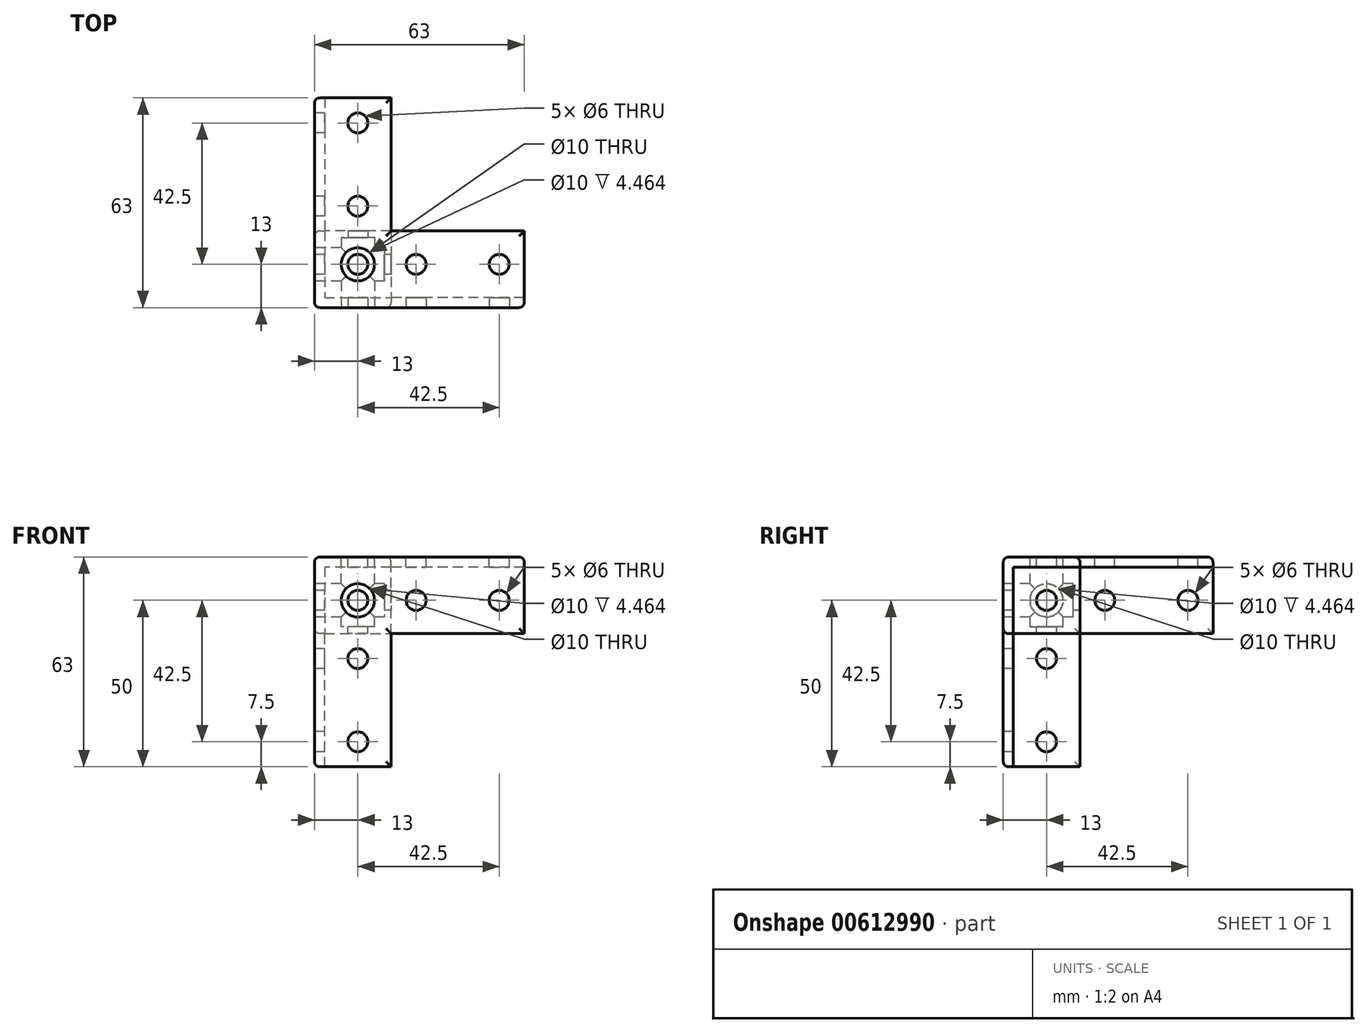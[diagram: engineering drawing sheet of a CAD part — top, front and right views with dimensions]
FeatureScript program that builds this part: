
annotation { "Feature Type Name" : "Feature", "Feature Type Description" : "" }
export const myFeature = defineFeature(function(context is Context, id is Id, definition is map)
    precondition{}
    {
        {
            var Q0;
            Q0=qCreatedBy(makeId("Front.planeOp"),FACE);
            var sketch = newSketch(context, id + "F0", { "sketchPlane" : qUnion([Q0])});
            skLineSegment(sketch, "E0", {"start": v(0, 0) * mm, "end": v(0, 40) * mm});
            skLineSegment(sketch, "E1", {"start": v(0, 0) * mm, "end": v(-20, 0) * mm});
            skLineSegment(sketch, "E2", {"start": v(-20, 0) * mm, "end": v(-20, 40) * mm});
            skLineSegment(sketch, "E3", {"start": v(-20, 40) * mm, "end": v(0, 40) * mm});
            skLineSegment(sketch, "E4", {"start": v(-20, 40) * mm, "end": v(-23, 40) * mm});
            skLineSegment(sketch, "E5", {"start": v(-23, 40) * mm, "end": v(-23, 0) * mm});
            skLineSegment(sketch, "E6", {"start": v(-23, 0) * mm, "end": v(-20, 0) * mm});
            skCircle(sketch, "E7", {"center": v(-10, 32.5) * mm, "radius": 3 * mm});
            skCircle(sketch, "E8", {"center": v(-10, 7.5) * mm, "radius": 3 * mm});
            skLineSegment(sketch, "E9", {"start": v(-10, 40) * mm, "end": v(-10, 0) * mm, "construction": true});
            skLineSegment(sketch, "E10", {"start": v(0, 40) * mm, "end": v(0, 60) * mm});
            skLineSegment(sketch, "E11", {"start": v(0, 60) * mm, "end": v(-20, 60) * mm});
            skLineSegment(sketch, "E12", {"start": v(-20, 60) * mm, "end": v(-20, 40) * mm});
            skLineSegment(sketch, "E13", {"start": v(-23, 40) * mm, "end": v(-23, 60) * mm});
            skLineSegment(sketch, "E14", {"start": v(-23, 60) * mm, "end": v(-20, 60) * mm});
            skLineSegment(sketch, "E15", {"start": v(0, 60) * mm, "end": v(40, 60) * mm});
            skLineSegment(sketch, "E16", {"start": v(40, 60) * mm, "end": v(40, 40) * mm});
            skLineSegment(sketch, "E17", {"start": v(40, 40) * mm, "end": v(0, 40) * mm});
            skLineSegment(sketch, "E18", {"start": v(-20, 50) * mm, "end": v(40, 50) * mm, "construction": true});
            skCircle(sketch, "E19", {"center": v(7.5, 50) * mm, "radius": 3 * mm});
            skCircle(sketch, "E20", {"center": v(32.5, 50) * mm, "radius": 3 * mm});
            skCircle(sketch, "E21", {"center": v(-10, 50) * mm, "radius": 5 * mm});
            skLineSegment(sketch, "E22", {"start": v(-23, 60) * mm, "end": v(-23, 63) * mm});
            skLineSegment(sketch, "E23", {"start": v(-23, 63) * mm, "end": v(40, 63) * mm});
            skLineSegment(sketch, "E24", {"start": v(40, 63) * mm, "end": v(40, 60) * mm});
            skLineSegment(sketch, "E25", {"start": v(0, 60) * mm, "end": v(0, 63) * mm});
            skSolve(sketch);
        }
        {
            var Q0;
            Q0=makeQuery(id+"F0.imprint","IMPRINT",FACE,{"disambiguationData":[TD([[makeQuery(id+"F0.imprint","IMPRINT",EDGE,{"derivedFrom":sQuery(id+"F0.wireOp",EDGE,"E0")}),1.0]])]});
            var Q1;
            Q1=makeQuery(id+"F0.imprint","IMPRINT",FACE,{"disambiguationData":[TD([[makeQuery(id+"F0.imprint","IMPRINT",EDGE,{"derivedFrom":sQuery(id+"F0.wireOp",EDGE,"E3")}),1.0]])]});
            var Q2;
            Q2=makeQuery(id+"F0.imprint","IMPRINT",FACE,{"disambiguationData":[TD([[makeQuery(id+"F0.imprint","IMPRINT",EDGE,{"derivedFrom":sQuery(id+"F0.wireOp",EDGE,"E10")}),-1.0]])]});
            extrude(context, id + "F1", {"entities" : qUnion([Q0, Q1, Q2]), "oppositeDirection" : true, "depth" : 3 * mm, "offsetDistance" : 25 * mm});
        }
        {
            var Q0;
            Q0=makeQuery(id+"F0.imprint","IMPRINT",FACE,{"disambiguationData":[TD([[makeQuery(id+"F0.imprint","IMPRINT",EDGE,{"derivedFrom":sQuery(id+"F0.wireOp",EDGE,"E2")}),1.0]])]});
            var Q1;
            Q1=makeQuery(id+"F0.imprint","IMPRINT",FACE,{"disambiguationData":[TD([[makeQuery(id+"F0.imprint","IMPRINT",EDGE,{"derivedFrom":sQuery(id+"F0.wireOp",EDGE,"E15")}),1.0]])]});
            extrude(context, id + "F2", {"entities" : qUnion([Q0, Q1]), "operationType" : NewBodyOperationType.ADD, "oppositeDirection" : true, "depth" : 23 * mm, "offsetDistance" : 25 * mm});
        }
        {
            var Q0;
            Q0=makeQuery(id+"F0.imprint","IMPRINT",FACE,{"disambiguationData":[TD([[makeQuery(id+"F0.imprint","IMPRINT",EDGE,{"derivedFrom":sQuery(id+"F0.wireOp",EDGE,"E11")}),-1.0]])]});
            var Q1;
            Q1=makeQuery(id+"F0.imprint","IMPRINT",FACE,{"disambiguationData":[TD([[makeQuery(id+"F0.imprint","IMPRINT",EDGE,{"derivedFrom":sQuery(id+"F0.wireOp",EDGE,"E4")}),-1.0]])]});
            extrude(context, id + "F3", {"entities" : qUnion([Q0, Q1]), "operationType" : NewBodyOperationType.ADD, "oppositeDirection" : true, "depth" : 63 * mm, "offsetDistance" : 25 * mm});
        }
        {
            var Q0;
            {var subQ0=sQuery(id+"F0.wireOp",EDGE,"E23");Q0=makeQuery(id+"F3.boolean.opBoolean","MERGE",FACE,{"derivedFrom":[makeQuery(id+"F2.opExtrude","SWEPT_FACE",FACE,{"disambiguationData":[OSD([subQ0])]}),makeQuery(id+"F3.opExtrude","SWEPT_FACE",FACE,{"disambiguationData":[OSD([subQ0])]})]});}
            var sketch = newSketch(context, id + "F4", { "sketchPlane" : qUnion([Q0])});
            skCircle(sketch, "E26", {"center": v(-10, 55.5) * mm, "radius": 3 * mm});
            skCircle(sketch, "E27", {"center": v(-10, 30.5) * mm, "radius": 3 * mm});
            skCircle(sketch, "E28", {"center": v(-10, 13) * mm, "radius": 5 * mm});
            skCircle(sketch, "E29", {"center": v(7.5, 13) * mm, "radius": 3 * mm});
            skCircle(sketch, "E30", {"center": v(32.5, 13) * mm, "radius": 3 * mm});
            skLineSegment(sketch, "E31", {"start": v(-10, 63) * mm, "end": v(-10, 0) * mm, "construction": true});
            skLineSegment(sketch, "E32", {"start": v(40, 13) * mm, "end": v(-10, 13) * mm, "construction": true});
            skLineSegment(sketch, "E33", {"start": v(0, 23) * mm, "end": v(0, 0) * mm, "construction": true});
            skSolve(sketch);
        }
        {
            var Q0;
            Q0=makeQuery(id+"F3.boolean.opBoolean","MERGE",FACE,{"derivedFrom":[makeQuery(id+"F2.opExtrude","SWEPT_FACE",FACE,{"disambiguationData":[OSD([sQuery(id+"F0.wireOp",EDGE,"E5")])]}),makeQuery(id+"F3.opExtrude","SWEPT_FACE",FACE,{"disambiguationData":[OSD([sQuery(id+"F0.wireOp",EDGE,"E13"),sQuery(id+"F0.wireOp",EDGE,"E22")])]})]});
            var sketch = newSketch(context, id + "F5", { "sketchPlane" : qUnion([Q0])});
            skLineSegment(sketch, "E34", {"start": v(-63, 50) * mm, "end": v(0, 50) * mm, "construction": true});
            skLineSegment(sketch, "E35", {"start": v(-13, 0) * mm, "end": v(-13, 50) * mm, "construction": true});
            skLineSegment(sketch, "E36", {"start": v(-23, 40) * mm, "end": v(0, 40) * mm, "construction": true});
            skLineSegment(sketch, "E37", {"start": v(-23, 40) * mm, "end": v(-23, 63) * mm, "construction": true});
            skCircle(sketch, "E38", {"center": v(-13, 50) * mm, "radius": 5 * mm});
            skCircle(sketch, "E39", {"center": v(-30.5, 50) * mm, "radius": 3 * mm});
            skCircle(sketch, "E40", {"center": v(-55.5, 50) * mm, "radius": 3 * mm});
            skCircle(sketch, "E41", {"center": v(-13, 32.5) * mm, "radius": 3 * mm});
            skCircle(sketch, "E42", {"center": v(-13, 7.5) * mm, "radius": 3 * mm});
            skSolve(sketch);
        }
        {
            var Q0;
            Q0=makeQuery(id+"F4.imprint","IMPRINT",FACE,{"disambiguationData":[TD([[makeQuery(id+"F4.imprint","IMPRINT",EDGE,{"derivedFrom":sQuery(id+"F4.wireOp",EDGE,"E26")}),1.0]])]});
            var Q1;
            Q1=makeQuery(id+"F4.imprint","IMPRINT",FACE,{"disambiguationData":[TD([[makeQuery(id+"F4.imprint","IMPRINT",EDGE,{"derivedFrom":sQuery(id+"F4.wireOp",EDGE,"E27")}),1.0]])]});
            var Q2;
            Q2=makeQuery(id+"F4.imprint","IMPRINT",FACE,{"disambiguationData":[TD([[makeQuery(id+"F4.imprint","IMPRINT",EDGE,{"derivedFrom":sQuery(id+"F4.wireOp",EDGE,"E28")}),1.0]])]});
            var Q3;
            Q3=makeQuery(id+"F4.imprint","IMPRINT",FACE,{"disambiguationData":[TD([[makeQuery(id+"F4.imprint","IMPRINT",EDGE,{"derivedFrom":sQuery(id+"F4.wireOp",EDGE,"E29")}),1.0]])]});
            var Q4;
            Q4=makeQuery(id+"F4.imprint","IMPRINT",FACE,{"disambiguationData":[TD([[makeQuery(id+"F4.imprint","IMPRINT",EDGE,{"derivedFrom":sQuery(id+"F4.wireOp",EDGE,"E30")}),1.0]])]});
            extrude(context, id + "F6", {"entities" : qUnion([Q0, Q1, Q2, Q3, Q4]), "operationType" : NewBodyOperationType.REMOVE, "oppositeDirection" : true, "depth" : 25 * mm, "offsetDistance" : 25 * mm});
        }
        {
            var Q0;
            Q0=makeQuery(id+"F5.imprint","IMPRINT",FACE,{"disambiguationData":[TD([[makeQuery(id+"F5.imprint","IMPRINT",EDGE,{"derivedFrom":sQuery(id+"F5.wireOp",EDGE,"E40")}),1.0]])]});
            var Q1;
            Q1=makeQuery(id+"F5.imprint","IMPRINT",FACE,{"disambiguationData":[TD([[makeQuery(id+"F5.imprint","IMPRINT",EDGE,{"derivedFrom":sQuery(id+"F5.wireOp",EDGE,"E39")}),1.0]])]});
            var Q2;
            Q2=makeQuery(id+"F5.imprint","IMPRINT",FACE,{"disambiguationData":[TD([[makeQuery(id+"F5.imprint","IMPRINT",EDGE,{"derivedFrom":sQuery(id+"F5.wireOp",EDGE,"E38")}),1.0]])]});
            var Q3;
            Q3=makeQuery(id+"F5.imprint","IMPRINT",FACE,{"disambiguationData":[TD([[makeQuery(id+"F5.imprint","IMPRINT",EDGE,{"derivedFrom":sQuery(id+"F5.wireOp",EDGE,"E42")}),1.0]])]});
            var Q4;
            Q4=makeQuery(id+"F5.imprint","IMPRINT",FACE,{"disambiguationData":[TD([[makeQuery(id+"F5.imprint","IMPRINT",EDGE,{"derivedFrom":sQuery(id+"F5.wireOp",EDGE,"E41")}),1.0]])]});
            extrude(context, id + "F7", {"entities" : qUnion([Q0, Q1, Q2, Q3, Q4]), "operationType" : NewBodyOperationType.REMOVE, "oppositeDirection" : true, "depth" : 25 * mm, "offsetDistance" : 25 * mm});
        }
        {
            var Q0;
            Q0=makeQuery(id+"F0.imprint","IMPRINT",FACE,{"disambiguationData":[TD([[makeQuery(id+"F0.imprint","IMPRINT",EDGE,{"derivedFrom":sQuery(id+"F0.wireOp",EDGE,"E3")}),1.0]])]});
            var Q1;
            Q1=makeQuery(id+"F0.imprint","IMPRINT",FACE,{"disambiguationData":[TD([[makeQuery(id+"F0.imprint","IMPRINT",EDGE,{"derivedFrom":sQuery(id+"F0.wireOp",EDGE,"E11")}),-1.0]])]});
            var Q2;
            Q2=makeQuery(id+"F0.imprint","IMPRINT",FACE,{"disambiguationData":[TD([[makeQuery(id+"F0.imprint","IMPRINT",EDGE,{"derivedFrom":sQuery(id+"F0.wireOp",EDGE,"E4")}),-1.0]])]});
            var Q3;
            Q3=makeQuery(id+"F0.imprint","IMPRINT",FACE,{"disambiguationData":[TD([[makeQuery(id+"F0.imprint","IMPRINT",EDGE,{"derivedFrom":sQuery(id+"F0.wireOp",EDGE,"E21")}),1.0]])]});
            extrude(context, id + "F8", {"entities" : qUnion([Q0, Q1, Q2, Q3]), "operationType" : NewBodyOperationType.ADD, "oppositeDirection" : true, "depth" : 23 * mm, "offsetDistance" : 25 * mm});
        }
        {
            var Q0;
            Q0=sQuery(id+"F0.wireOp",VERTEX,"E21.center");
            var Q1;
            Q1=sQuery(id+"F5.wireOp",VERTEX,"E38.center");
            var Q2;
            Q2=sQuery(id+"F4.wireOp",VERTEX,"E28.center");
            var Q3;
            Q3=makeQuery(id+"F1.opExtrude","SWEPT_BODY",BODY,{"disambiguationData":[OSD([sQuery(id+"F0.wireOp",EDGE,"E0"),sQuery(id+"F0.wireOp",EDGE,"E1"),sQuery(id+"F0.wireOp",EDGE,"E2"),sQuery(id+"F0.wireOp",EDGE,"E7"),sQuery(id+"F0.wireOp",EDGE,"E8"),sQuery(id+"F0.wireOp",EDGE,"E11"),sQuery(id+"F0.wireOp",EDGE,"E12"),sQuery(id+"F0.wireOp",EDGE,"E15"),sQuery(id+"F0.wireOp",EDGE,"E16"),sQuery(id+"F0.wireOp",EDGE,"E17"),sQuery(id+"F0.wireOp",EDGE,"E19"),sQuery(id+"F0.wireOp",EDGE,"E20"),sQuery(id+"F0.wireOp",EDGE,"E21")])]});
            hole(context, id + "F9", {"style" : HoleStyle.C_BORE, "endStyle" : HoleEndStyle.BLIND, "holeDiameter" : 6 * mm, "cBoreDiameter" : 10 * mm, "cBoreDepth" : 21 * mm, "majorDiameter" : 5 * mm, "holeDepth" : 23 * mm, "isTappedThrough" : true, "tappedDepth" : 12 * mm, "tapClearance" : 3, "locations" : qUnion([Q0, Q1, Q2]), "scope" : qUnion([Q3])});
        }
        {
            var Q0;
            Q0=makeQuery(id+"F3.boolean.opBoolean","MERGE",EDGE,{"derivedFrom":[makeQuery(id+"F2.opExtrude","CAP_EDGE",EDGE,{"disambiguationData":[OSD([sQuery(id+"F0.wireOp",EDGE,"E5")])],"isStart":true}),makeQuery(id+"F3.opExtrude","CAP_EDGE",EDGE,{"disambiguationData":[OSD([sQuery(id+"F0.wireOp",EDGE,"E13"),sQuery(id+"F0.wireOp",EDGE,"E22")])],"isStart":true})]});
            var Q1;
            {var subQ0=sQuery(id+"F0.wireOp",EDGE,"E23");Q1=makeQuery(id+"F3.boolean.opBoolean","MERGE",EDGE,{"derivedFrom":[makeQuery(id+"F2.opExtrude","CAP_EDGE",EDGE,{"disambiguationData":[OSD([subQ0])],"isStart":true}),makeQuery(id+"F3.opExtrude","CAP_EDGE",EDGE,{"disambiguationData":[OSD([subQ0])],"isStart":true})]});}
            var Q2;
            Q2=makeQuery(id+"F3.opExtrude","SWEPT_EDGE",EDGE,{"disambiguationData":[OSD([sQuery(id+"F0.wireOp",EDGE,"E22"),sQuery(id+"F0.wireOp",EDGE,"E23")])]});
            var Q3;
            Q3=makeQuery(id+"F1.opExtrude","CAP_EDGE",EDGE,{"disambiguationData":[OSD([sQuery(id+"F0.wireOp",EDGE,"E17")])],"isStart":true});
            var Q4;
            Q4=makeQuery(id+"F1.opExtrude","CAP_EDGE",EDGE,{"disambiguationData":[OSD([sQuery(id+"F0.wireOp",EDGE,"E0")])],"isStart":true});
            var Q5;
            Q5=makeQuery(id+"F2.boolean.opBoolean","MERGE",EDGE,{"derivedFrom":[makeQuery(id+"F1.opExtrude","CAP_EDGE",EDGE,{"disambiguationData":[OSD([sQuery(id+"F0.wireOp",EDGE,"E1")])],"isStart":true}),makeQuery(id+"F2.opExtrude","CAP_EDGE",EDGE,{"disambiguationData":[OSD([sQuery(id+"F0.wireOp",EDGE,"E6")])],"isStart":true})]});
            var Q6;
            Q6=makeQuery(id+"F2.opExtrude","SWEPT_EDGE",EDGE,{"disambiguationData":[OSD([sQuery(id+"F0.wireOp",EDGE,"E5"),sQuery(id+"F0.wireOp",EDGE,"E6")])]});
            var Q7;
            Q7=makeQuery(id+"F2.opExtrude","CAP_EDGE",EDGE,{"disambiguationData":[OSD([sQuery(id+"F0.wireOp",EDGE,"E5")])],"isStart":false});
            var Q8;
            Q8=makeQuery(id+"F3.opExtrude","SWEPT_EDGE",EDGE,{"disambiguationData":[OSD([sQuery(id+"F0.wireOp",EDGE,"E4"),sQuery(id+"F0.wireOp",EDGE,"E5"),sQuery(id+"F0.wireOp",EDGE,"E13")])]});
            var Q9;
            Q9=makeQuery(id+"F3.opExtrude","CAP_EDGE",EDGE,{"disambiguationData":[OSD([sQuery(id+"F0.wireOp",EDGE,"E13"),sQuery(id+"F0.wireOp",EDGE,"E22")])],"isStart":false});
            var Q10;
            Q10=makeQuery(id+"F3.opExtrude","CAP_EDGE",EDGE,{"disambiguationData":[OSD([sQuery(id+"F0.wireOp",EDGE,"E23")])],"isStart":false});
            var Q11;
            Q11=makeQuery(id+"F3.opExtrude","SWEPT_EDGE",EDGE,{"disambiguationData":[OSD([sQuery(id+"F0.wireOp",EDGE,"E23"),sQuery(id+"F0.wireOp",EDGE,"E25")])]});
            var Q12;
            Q12=makeQuery(id+"F2.opExtrude","CAP_EDGE",EDGE,{"disambiguationData":[OSD([sQuery(id+"F0.wireOp",EDGE,"E23")])],"isStart":false});
            var Q13;
            Q13=makeQuery(id+"F2.opExtrude","SWEPT_EDGE",EDGE,{"disambiguationData":[OSD([sQuery(id+"F0.wireOp",EDGE,"E23"),sQuery(id+"F0.wireOp",EDGE,"E24")])]});
            var Q14;
            Q14=makeQuery(id+"F2.boolean.opBoolean","MERGE",EDGE,{"derivedFrom":[makeQuery(id+"F1.opExtrude","CAP_EDGE",EDGE,{"disambiguationData":[OSD([sQuery(id+"F0.wireOp",EDGE,"E16")])],"isStart":true}),makeQuery(id+"F2.opExtrude","CAP_EDGE",EDGE,{"disambiguationData":[OSD([sQuery(id+"F0.wireOp",EDGE,"E24")])],"isStart":true})]});
            var Q15;
            Q15=makeQuery(id+"F9.hole-2.boolean.opBoolean","INTERSECT",EDGE,{"disambiguationData":[OD(1.0)],"derivedFrom":[makeQuery(id+"F9.hole-0.boolean.opBoolean","COPY",FACE,{"derivedFrom":makeQuery(id+"F9.hole-0.opRevolve","SWEPT_FACE",FACE,{"disambiguationData":[OSD([sQuery(id+"F9.hole-0.sketch.wireOp",EDGE,"cbore_start_line_2")])]})}),makeQuery(id+"F9.hole-2.opRevolve","SWEPT_FACE",FACE,{"disambiguationData":[OSD([sQuery(id+"F9.hole-2.sketch.wireOp",EDGE,"cbore_start_line_2")])]})]});
            var Q16;
            Q16=makeQuery(id+"F9.hole-2.boolean.opBoolean","SPLIT",EDGE,{"disambiguationData":[OD(1.0)],"derivedFrom":makeQuery(id+"F9.hole-1.boolean.opBoolean","INTERSECT",EDGE,{"derivedFrom":[makeQuery(id+"F9.hole-0.boolean.opBoolean","COPY",FACE,{"derivedFrom":makeQuery(id+"F9.hole-0.opRevolve","SWEPT_FACE",FACE,{"disambiguationData":[OSD([sQuery(id+"F9.hole-0.sketch.wireOp",EDGE,"cbore_start_line_2")])]})}),makeQuery(id+"F9.hole-1.opRevolve","SWEPT_FACE",FACE,{"disambiguationData":[OSD([sQuery(id+"F9.hole-1.sketch.wireOp",EDGE,"cbore_start_line_2")])]})]})});
            var Q17;
            Q17=makeQuery(id+"F9.hole-2.boolean.opBoolean","INTERSECT",EDGE,{"disambiguationData":[OD(0.0)],"derivedFrom":[makeQuery(id+"F9.hole-0.boolean.opBoolean","COPY",FACE,{"derivedFrom":makeQuery(id+"F9.hole-0.opRevolve","SWEPT_FACE",FACE,{"disambiguationData":[OSD([sQuery(id+"F9.hole-0.sketch.wireOp",EDGE,"cbore_start_line_2")])]})}),makeQuery(id+"F9.hole-2.opRevolve","SWEPT_FACE",FACE,{"disambiguationData":[OSD([sQuery(id+"F9.hole-2.sketch.wireOp",EDGE,"cbore_start_line_2")])]})]});
            var Q18;
            Q18=makeQuery(id+"F9.hole-2.boolean.opBoolean","SPLIT",EDGE,{"disambiguationData":[OD(0.0)],"derivedFrom":makeQuery(id+"F9.hole-1.boolean.opBoolean","INTERSECT",EDGE,{"derivedFrom":[makeQuery(id+"F9.hole-0.boolean.opBoolean","COPY",FACE,{"derivedFrom":makeQuery(id+"F9.hole-0.opRevolve","SWEPT_FACE",FACE,{"disambiguationData":[OSD([sQuery(id+"F9.hole-0.sketch.wireOp",EDGE,"cbore_start_line_2")])]})}),makeQuery(id+"F9.hole-1.opRevolve","SWEPT_FACE",FACE,{"disambiguationData":[OSD([sQuery(id+"F9.hole-1.sketch.wireOp",EDGE,"cbore_start_line_2")])]})]})});
            var Q19;
            Q19=makeQuery(id+"F9.hole-2.boolean.opBoolean","INTERSECT",EDGE,{"disambiguationData":[OD(2.0)],"derivedFrom":[makeQuery(id+"F9.hole-0.boolean.opBoolean","COPY",FACE,{"derivedFrom":makeQuery(id+"F9.hole-0.opRevolve","SWEPT_FACE",FACE,{"disambiguationData":[OSD([sQuery(id+"F9.hole-0.sketch.wireOp",EDGE,"cbore_start_line_2")])]})}),makeQuery(id+"F9.hole-2.opRevolve","SWEPT_FACE",FACE,{"disambiguationData":[OSD([sQuery(id+"F9.hole-2.sketch.wireOp",EDGE,"cbore_start_line_2")])]})]});
            var Q20;
            Q20=makeQuery(id+"F9.hole-2.boolean.opBoolean","SPLIT",EDGE,{"disambiguationData":[OD(2.0)],"derivedFrom":makeQuery(id+"F9.hole-1.boolean.opBoolean","INTERSECT",EDGE,{"derivedFrom":[makeQuery(id+"F9.hole-0.boolean.opBoolean","COPY",FACE,{"derivedFrom":makeQuery(id+"F9.hole-0.opRevolve","SWEPT_FACE",FACE,{"disambiguationData":[OSD([sQuery(id+"F9.hole-0.sketch.wireOp",EDGE,"cbore_start_line_2")])]})}),makeQuery(id+"F9.hole-1.opRevolve","SWEPT_FACE",FACE,{"disambiguationData":[OSD([sQuery(id+"F9.hole-1.sketch.wireOp",EDGE,"cbore_start_line_2")])]})]})});
            var Q21;
            Q21=makeQuery(id+"F9.hole-2.boolean.opBoolean","INTERSECT",EDGE,{"disambiguationData":[OD(2.0)],"derivedFrom":[makeQuery(id+"F9.hole-1.boolean.opBoolean","COPY",FACE,{"derivedFrom":makeQuery(id+"F9.hole-1.opRevolve","SWEPT_FACE",FACE,{"disambiguationData":[OSD([sQuery(id+"F9.hole-1.sketch.wireOp",EDGE,"cbore_start_line_2")])]})}),makeQuery(id+"F9.hole-2.opRevolve","SWEPT_FACE",FACE,{"disambiguationData":[OSD([sQuery(id+"F9.hole-2.sketch.wireOp",EDGE,"cbore_start_line_2")])]})]});
            fillet(context, id + "F10", {"entities" : qUnion([Q0, Q1, Q2, Q3, Q4, Q5, Q6, Q7, Q8, Q9, Q10, Q11, Q12, Q13, Q14, Q15, Q16, Q17, Q18, Q19, Q20, Q21]), "radius" : 1.5 * mm, "tangentPropagation" : true, "allowEdgeOverflow" : false});
        }
    });
